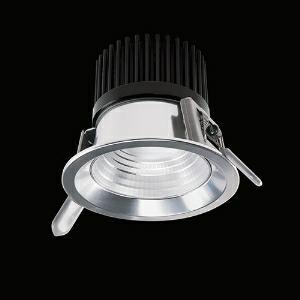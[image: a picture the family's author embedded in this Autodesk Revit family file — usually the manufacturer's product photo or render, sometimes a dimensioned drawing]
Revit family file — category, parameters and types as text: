
# Revit family: spectral_myral_myral_3500-840-f
name_source: partatom
category: Lighting Fixtures
revit_build: Autodesk Revit 2016 (Build: 20150220_1215(x64)
units: mm (PartAtom-declared; Revit-internal decimal feet)

## family parameters
Cut with Voids When Loaded = No
Host = Face
Light Source = No
Part Type = Normal
Room Calculation Point = No
Round Connector Dimension = Use Diameter
Shared = No

## types (1)
- SPECTRAL MYRAL (1 x )
    Apparent Load = 0 VA
    Approval mark = CE
    CIE Flux Codes = 81 99 100 100 100
    Control Gear = Electronic transformer
    Default Elevation = 1800 mm
    Description = SPG0320187
MYRAL recessed spot

Design:
    Height = 0 mm  [stored 0 ft]
    Lamp = 1 x
    Lamp count = 1
    Length = 120 mm
    Luminous efficacy = 0 lm/W
    Manufacturer = Ridi
    ModVariant = No
    Model = MYRAL 3500-840-F
    Mounting Place = Ceiling
    Mounting Type = Recessed
    Number of Poles = 1
    OnlyDefault = Yes
    Power Factor = 1
    Product Name = SPECTRAL MYRAL
    Product group = Downlight recessed
    ProductGroupID = 400
    Protection Class = Protection class
    Protection Degree = IP 20
    RlxData = <blob elided: 38885 chars, md5=445dc82b>
    Socket = socket
    Standby Power = 0 W
    System Light Flux = 0 lm
    System Power = 0 W
    Type Image = myral_04.jpg
    URL = http://reluxnet.relux.com
    VarID = ---
    Voltage = 0 V
    Weight = 0.00 kg
    Width = 0 mm  [stored 0 ft]

note: [stored X ft] marks values corroborated as IEEE doubles in the binary element streams (Revit-internal decimal feet)

## geometry (parser evidence)
native form markers: Sweep x8
no freeform markers — native parametric forms only
